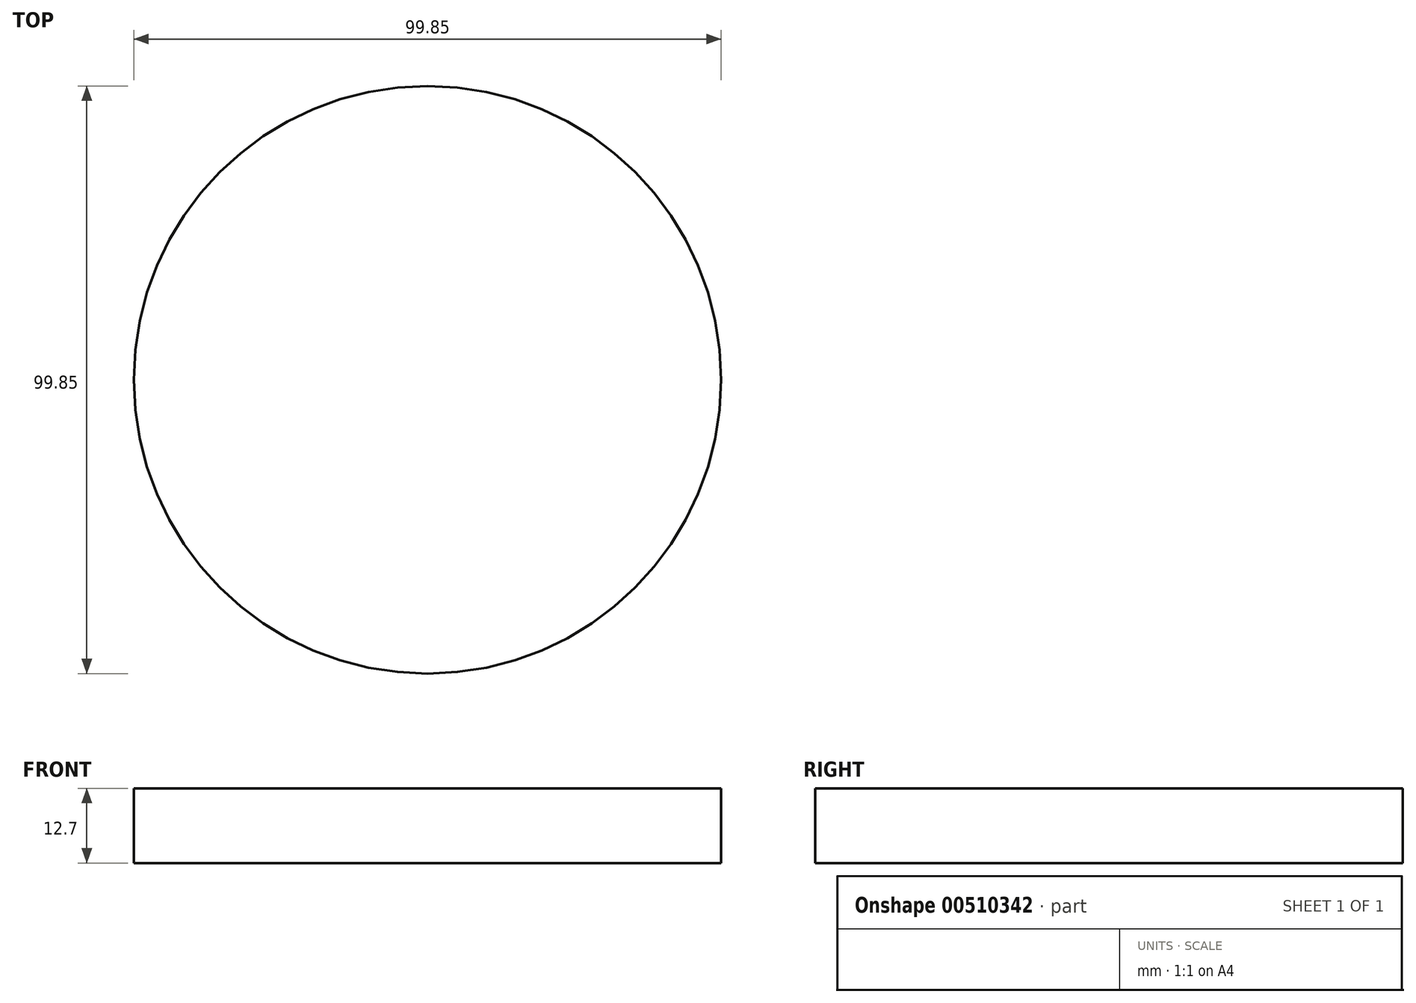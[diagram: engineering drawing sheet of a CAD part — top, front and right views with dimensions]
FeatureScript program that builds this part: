
annotation { "Feature Type Name" : "Feature", "Feature Type Description" : "" }
export const myFeature = defineFeature(function(context is Context, id is Id, definition is map)
    precondition{}
    {
        {
            var Q0;
            Q0=qCreatedBy(makeId("Top.planeOp"),FACE);
            var sketch = newSketch(context, id + "F0", { "sketchPlane" : qUnion([Q0])});
            skCircle(sketch, "E0", {"center": v(17.52, -28.1) * mm, "radius": 49.93 * mm});
            skSolve(sketch);
        }
        {
            var Q0;
            Q0 = qSketchRegion(id + "F0", true);
            extrude(context, id + "F1", {"entities" : qUnion([Q0]), "depth" : 12.7 * mm});
        }
    });
